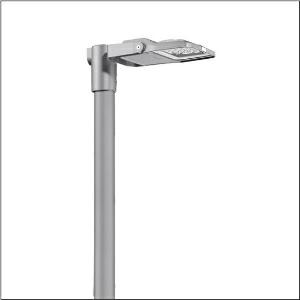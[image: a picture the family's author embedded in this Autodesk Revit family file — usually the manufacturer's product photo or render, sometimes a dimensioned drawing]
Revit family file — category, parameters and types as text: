
# Revit family: floodlight_fl_21_iq_micro___pl61_5xa7762a4c3a_196d
name_source: partatom
category: Lighting Fixtures
units: mm (PartAtom-declared; Revit-internal decimal feet)

## family parameters
Cut with Voids When Loaded = No
Host = Face
Light Source = No
Part Type = Normal
Room Calculation Point = No
Round Connector Dimension = Use Diameter
Shared = No

## types (1)
- --- (1 x LED, 3030 lm, 23.1 W, 4000K)
    Apparent Load = 23 VA
    CIE Flux Codes = 33 65 98 100 100
    Color Rendering = 70
    Color Temperature = 4000K
    Default Elevation = 1800 mm
    Description = Floodlight FL 21 iQ micro, floodlight, primary light control with lens, of PMMA, primary optical cover: protective disc, of toughened safety glass, transparent, light distribution: PL61, light emission: direct distribution, installation type: surface-mounted, LED, High Power LED, rated luminous flux: 3.030lm, luminous efficacy: 131lm/W, light colour: 740, colour temperature: 4000K, control: Auto-Match, Temp-Guard, Night-Set, Smart-Wire, Desk-Remote (wireless, voltage-free reading and setting of iQ features in the workshop via application-optimized NFC function/RFID function), optimised constant luminous flux control (CLO 2.0), Street-Remote, with terminal, 6-pole, mains connection: 220..240V, AC, 50/60Hz, start of lifetime: 23W, end of service life: 24W, reduction: 11W, luminaire housing, of diecast aluminium, powder-coated, Siteco® metallic grey (DB 702S), corrosivity category C5 mid according to DIN EN ISO 12944, sealing non-destructively replaceable, please order mast flange separately, mast bracket, of steel, galvanised, powder-coated, Siteco® metallic grey (DB 702S), protection rating (complete): IP66, insulation class (complete): insulation class II (safety insulation), certification: CE, ENEC, VDE, protection symbol: D, impact resistance: IK07, permissible operating ambient temperature: -40..+40°C, permissible operating ambient temperature for outdoor applications: -40..+50°C, standard: DIN EN 12944, LABS conformity tested according to VDMA 24364:2018-05, packaging unit: 1 piece

Light Distribution: PL61
    Height = 65 mm
    Lamp = 1 x LED
    Lamp Light Flux = 3030 lm
    Lamp Power = 23.1 W
    Lamp count = 1
    Length = 312 mm
    Luminous efficacy = 131 lm/W
    Manufacturer = Siteco
    ModVariant = No
    Model = 5XA7762A4C3A
    Number of Poles = 1
    OnlyDefault = Yes
    Power Factor = 1
    Product Name = Floodlight FL 21 iQ micro | PL61
    Product group = floodlight | pylon annexe
    ProductGroupID = 6200
    Protection Class = Protection class II
    Protection Degree = IP 66
    RLX_Detail_Level = 1
    RLX_Emergency_Light_Flux = 0 lm
    RLX_Emergency_Type = 0
    RLX_Emergency_Type_DB = No
    RlxData = <blob elided: 101985 chars, md5=664aa88d>
    Socket = socket
    Standby Power = 0 W
    System Light Flux = 3030 lm
    System Power = 23 W
    Type Comments = factory setting: luminous flux: 100 % | dim-lin: 254 | 455 mA
    Type Image = l_1007121.jpg
    URL = http://relux.com
    VarID = @adj_166945
    Voltage = 0 V
    Weight = 0.00 kg
    Width = 230 mm

## geometry (parser evidence)
native form markers: Blend x4, Sweep x12
no freeform markers — native parametric forms only
